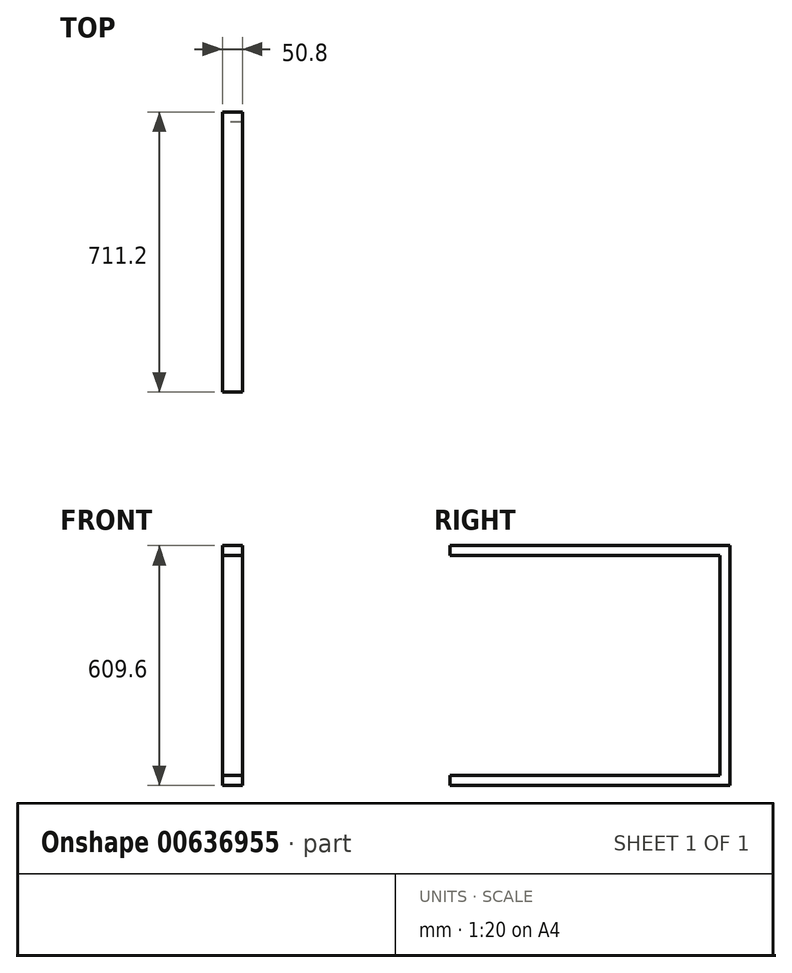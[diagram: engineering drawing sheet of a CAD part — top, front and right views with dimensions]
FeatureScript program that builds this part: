
annotation { "Feature Type Name" : "Feature", "Feature Type Description" : "" }
export const myFeature = defineFeature(function(context is Context, id is Id, definition is map)
    precondition{}
    {
        {
            var Q0;
            Q0=qCreatedBy(makeId("Top.planeOp"),FACE);
            var sketch = newSketch(context, id + "F0", { "sketchPlane" : qUnion([Q0])});
            skLineSegment(sketch, "E0.bottom", {"start": v(-564.29, -178.45) * mm, "end": v(-615.09, -178.45) * mm});
            skLineSegment(sketch, "E0.top", {"start": v(-564.29, 558.15) * mm, "end": v(-615.09, 558.15) * mm});
            skLineSegment(sketch, "E0.left", {"start": v(-564.29, -178.45) * mm, "end": v(-564.29, 558.15) * mm});
            skLineSegment(sketch, "E0.right", {"start": v(-615.09, -178.45) * mm, "end": v(-615.09, 558.15) * mm});
            skPoint(sketch, "E0.middle", {"position": v(-589.69, 189.85) * mm});
            skSolve(sketch);
        }
        {
            var Q0;
            Q0 = qSketchRegion(id + "F0", true);
            extrude(context, id + "F1", {"entities" : qUnion([Q0]), "depth" : 609.6 * mm, "offsetDistance" : 25.4 * mm});
        }
        {
            var Q0;
            Q0=makeQuery(id+"F1.opExtrude","SWEPT_FACE",FACE,{"disambiguationData":[OSD([sQuery(id+"F0.wireOp",EDGE,"E0.right")])]});
            var sketch = newSketch(context, id + "F2", { "sketchPlane" : qUnion([Q0])});
            skLineSegment(sketch, "E1.bottom", {"start": v(153.05, 25.4) * mm, "end": v(-532.75, 25.4) * mm});
            skLineSegment(sketch, "E1.top", {"start": v(153.05, 584.2) * mm, "end": v(-532.75, 584.2) * mm});
            skLineSegment(sketch, "E1.left", {"start": v(153.05, 25.4) * mm, "end": v(153.05, 584.2) * mm});
            skLineSegment(sketch, "E1.right", {"start": v(-532.75, 25.4) * mm, "end": v(-532.75, 584.2) * mm});
            skPoint(sketch, "E1.middle", {"position": v(-189.85, 304.8) * mm});
            skPoint(sketch, "E1.middle.positionSnap0", {"position": v(-558.15, 304.8) * mm});
            skPoint(sketch, "E1.middle.positionSnap1", {"position": v(-189.85, 609.6) * mm});
            skPoint(sketch, "E1.centerSnap0", {"position": v(-558.15, 304.8) * mm});
            skPoint(sketch, "E1.centerSnap1", {"position": v(-189.85, 609.6) * mm});
            skSolve(sketch);
        }
        {
            var Q0;
            Q0 = qSketchRegion(id + "F2", true);
            extrude(context, id + "F3", {"entities" : qUnion([Q0]), "operationType" : NewBodyOperationType.REMOVE, "oppositeDirection" : true, "depth" : 50.8 * mm, "offsetDistance" : 25.4 * mm});
        }
        {
            var Q0;
            Q0=makeQuery(id+"F1.opExtrude","SWEPT_FACE",FACE,{"disambiguationData":[OSD([sQuery(id+"F0.wireOp",EDGE,"E0.right")])]});
            var sketch = newSketch(context, id + "F4", { "sketchPlane" : qUnion([Q0])});
            skLineSegment(sketch, "E2.bottom", {"start": v(178.45, 609.6) * mm, "end": v(153.05, 609.6) * mm});
            skLineSegment(sketch, "E2.top", {"start": v(178.45, 0) * mm, "end": v(153.05, 0) * mm});
            skLineSegment(sketch, "E2.left", {"start": v(178.45, 609.6) * mm, "end": v(178.45, 0) * mm});
            skLineSegment(sketch, "E2.right", {"start": v(153.05, 609.6) * mm, "end": v(153.05, 0) * mm});
            skSolve(sketch);
        }
        {
            var Q0;
            {var subQ2=sQuery(id+"F4.wireOp",EDGE,"E2.bottom");Q0=makeQuery(id+"F4.imprint","IMPRINT",FACE,{"disambiguationData":[TD([[makeQuery(id+"F4.imprint","IMPRINT",EDGE,{"derivedFrom":subQ2}),1.0]])]});}
            extrude(context, id + "F5", {"entities" : qUnion([Q0]), "operationType" : NewBodyOperationType.REMOVE, "oppositeDirection" : true, "depth" : 50.8 * mm, "offsetDistance" : 25.4 * mm});
        }
    });
